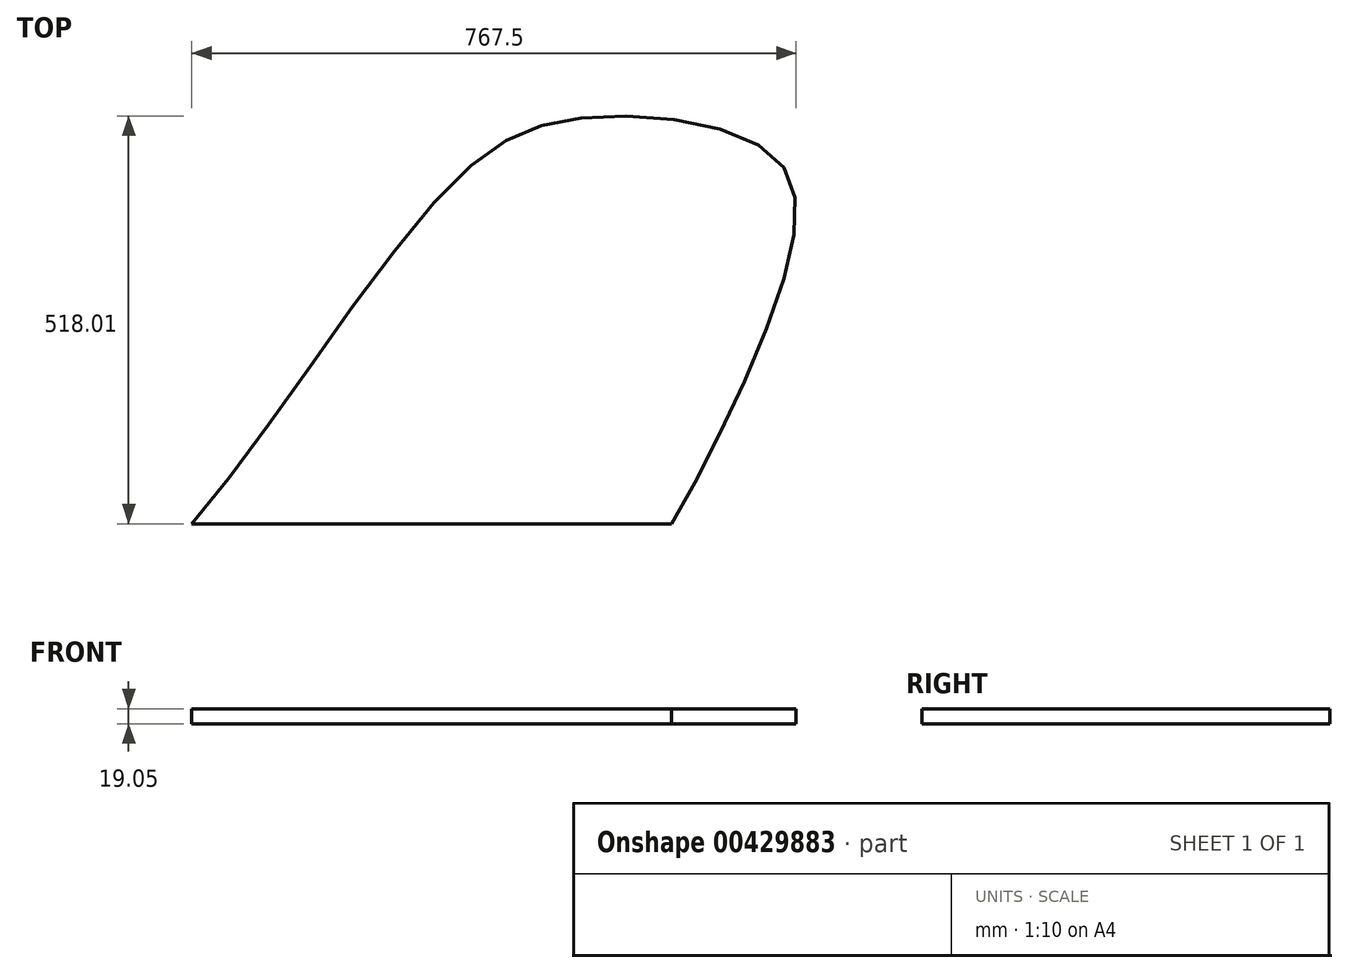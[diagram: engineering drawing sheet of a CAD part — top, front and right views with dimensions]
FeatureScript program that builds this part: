
annotation { "Feature Type Name" : "Feature", "Feature Type Description" : "" }
export const myFeature = defineFeature(function(context is Context, id is Id, definition is map)
    precondition{}
    {
        {
            var Q0;
            Q0=qCreatedBy(makeId("Top.planeOp"),FACE);
            var sketch = newSketch(context, id + "F0", { "sketchPlane" : qUnion([Q0])});
            skLineSegment(sketch, "E0", {"start": v(-51.97, 37.73) * mm, "end": v(557.63, 37.73) * mm});
            skFitSpline(sketch, "E1", {"points": [v(-51.97, 37.73) * mm, v(273.58, 464.87) * mm, v(459.58, 554.8) * mm, v(686.45, 505.75) * mm, v(702.8, 358.59) * mm, v(557.63, 37.73) * mm], "startDerivative": vector(1023.67, 1153.16) * mm, "endDerivative": vector(-626.2, -1062.01) * mm});
            skSolve(sketch);
        }
        {
            var Q0;
            Q0 = qSketchRegion(id + "F0", true);
            extrude(context, id + "F1", {"entities" : qUnion([Q0]), "depth" : 19.05 * mm});
        }
    });
